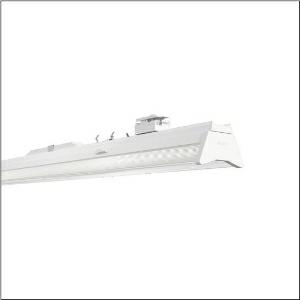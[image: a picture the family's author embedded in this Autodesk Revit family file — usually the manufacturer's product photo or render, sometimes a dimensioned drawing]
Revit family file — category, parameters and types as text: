
# Revit family: licross_r__21_performance_mo_52ts16dnd75f_76b1
name_source: partatom
category: Lighting Fixtures
units: mm (PartAtom-declared; Revit-internal decimal feet)

## family parameters
Cut with Voids When Loaded = No
Host = Face
Light Source = No
Part Type = Normal
Room Calculation Point = No
Round Connector Dimension = Use Diameter
Shared = No

## types (1)
- --- (1 x LED, 7810 lm, 60.9 W, 4000K)
    Apparent Load = 61 VA
    CIE Flux Codes = 66 88 96 79 100
    Color Rendering = 90
    Color Temperature = 4000K
    Default Elevation = 1800 mm
    Description = Licross® 21 Performance MO, luminaire insert, of sheet steel, galvanised, coil coated, white, length: 1.500mm, width: 120mm, height: 123mm, LED rated luminous flux: 7.810lm, light colour: 940, control gear: DALI 2, control gear: ECG DALI, with plug, 5-pole, with phase selection, mains connection: 220..240V, AC, 50/60Hz, halogen-free wiring, primary light control with lens, of plastic, primary optical cover: cover, of PMMA, light emission: direct/indirect distribution, protection rating (complete): IP50, insulation class (complete): insulation class I (protective earthing), certification: CE, ENEC, VDE, UKCA, protection symbol: D if used in an environment with non-conductive dust loads with corresponding accessories, permissible ambient temperature for indoor applications: -25..+40°C, corresponds to IFS (International Featured Standards) requirements for safety and quality in the food industry, reducing of maximum allowable ambient temperature of 5°C with ceiling mounting, packaging unit: 1 piece
    Height = 114 mm
    Lamp = 1 x LED
    Lamp Light Flux = 7810 lm
    Lamp Power = 60.9 W
    Lamp count = 1
    Length = 1500 mm
    Luminous efficacy = 128 lm/W
    Manufacturer = Siteco
    ModVariant = No
    Model = 52TS16DND75F
    Mounting Place = Ceiling
    Mounting Type = Pendant
    Number of Poles = 1
    OnlyDefault = Yes
    Power Factor = 1
    Product Name = Licross® 21 Performance MO
    Product group = luminaire insert
    ProductGroupID = 902
    Protection Class = Protection class I
    Protection Degree = IP 50
    RLX_Detail_Level = 1
    RlxData = <blob elided: 33905 chars, md5=2b3aec46>
    Socket = socket
    Standby Power = 0 W
    System Light Flux = 7810 lm
    System Power = 61 W
    Type Comments = factory setting: luminous flux: 100 % | dim-lin: 254 | 405 mA
    Type Image = l_1256138.jpg
    URL = http://relux.com
    VarID = @adj_129785
    Voltage = 0 V
    Weight = 0.00 kg
    Width = 120 mm

## geometry (parser evidence)
native form markers: Blend x4, Sweep x11
no freeform markers — native parametric forms only
